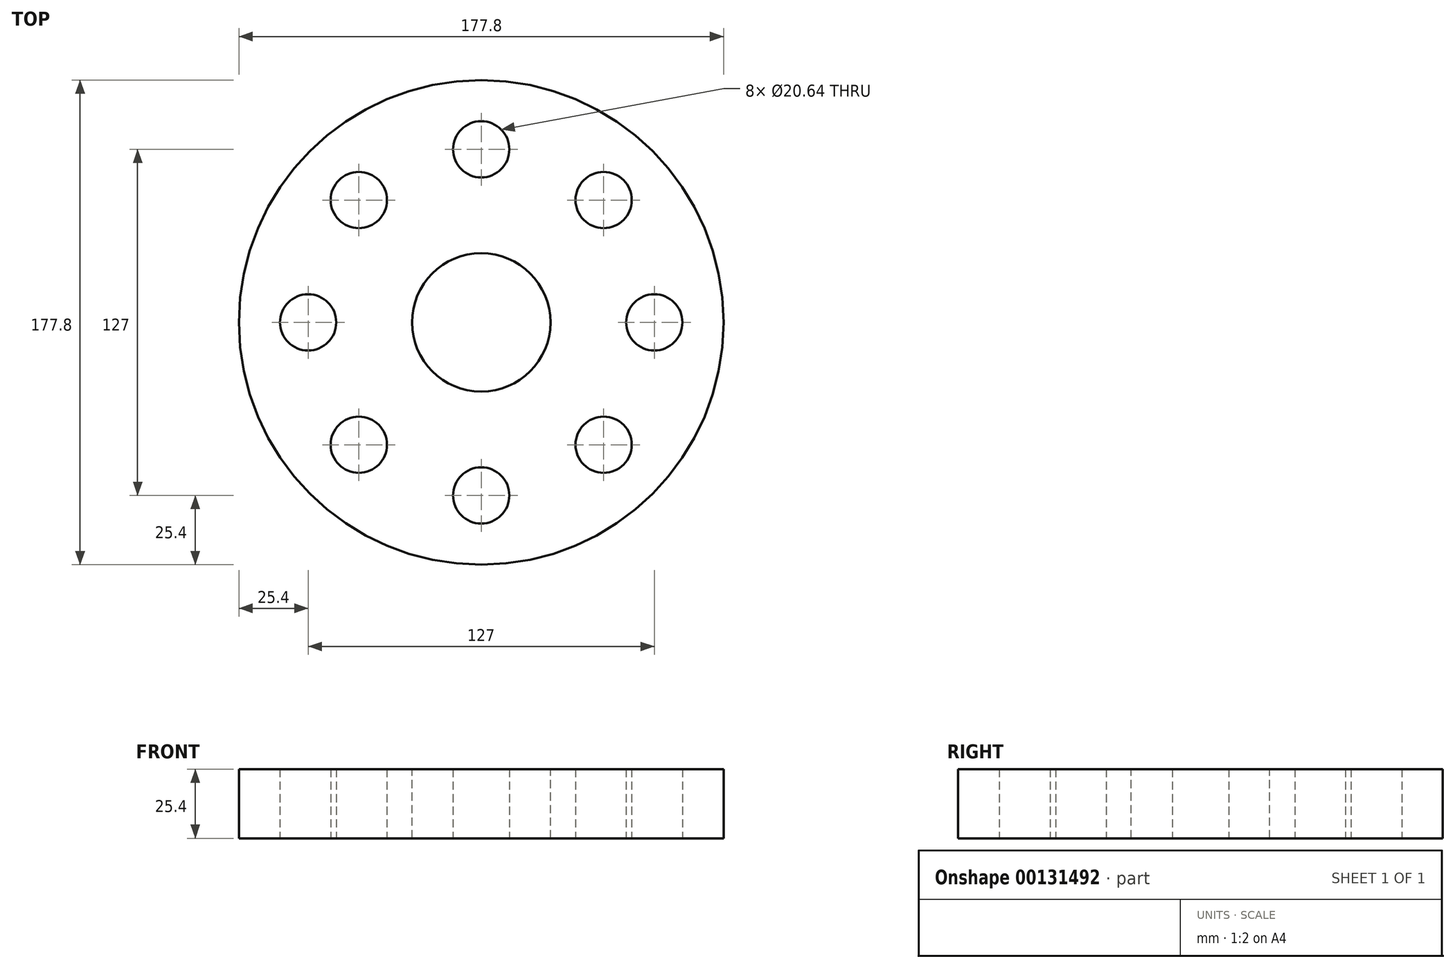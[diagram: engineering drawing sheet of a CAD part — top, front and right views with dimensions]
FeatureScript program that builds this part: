
annotation { "Feature Type Name" : "Feature", "Feature Type Description" : "" }
export const myFeature = defineFeature(function(context is Context, id is Id, definition is map)
    precondition{}
    {
        {
            var Q0;
            Q0=qCreatedBy(makeId("Top.planeOp"),FACE);
            var sketch = newSketch(context, id + "F0", { "sketchPlane" : qUnion([Q0])});
            skCircle(sketch, "E0", {"center": v(0, 0) * mm, "radius": 88.9 * mm});
            skPoint(sketch, "E1", {"position": v(0, 63.5) * mm});
            skPoint(sketch, "E2.1.0", {"position": v(-44.9, 44.9) * mm});
            skPoint(sketch, "E2.2.0", {"position": v(-63.5, 0) * mm});
            skPoint(sketch, "E3.0.3.0", {"position": v(-44.9, -44.9) * mm});
            skPoint(sketch, "E3.0.4.0", {"position": v(0, -63.5) * mm});
            skPoint(sketch, "E3.0.5.0", {"position": v(44.9, -44.9) * mm});
            skPoint(sketch, "E3.0.6.0", {"position": v(63.5, 0) * mm});
            skPoint(sketch, "E3.0.7.0", {"position": v(44.9, 44.9) * mm});
            skSolve(sketch);
        }
        {
            var Q0;
            Q0 = qSketchRegion(id + "F0", true);
            extrude(context, id + "F1", {"entities" : qUnion([Q0]), "depth" : 25.4 * mm});
        }
        {
            var Q0;
            Q0=sQuery(id+"F0.wireOp",VERTEX,"895da96b-3355-4bea-800d-bb29986c0918.1.0");
            var Q1;
            Q1=sQuery(id+"F0.wireOp",VERTEX,"E1");
            var Q2;
            Q2=sQuery(id+"F0.wireOp",VERTEX,"54c976e0-06ee-42b3-b940-04180ae81c69.0.7.0");
            var Q3;
            Q3=sQuery(id+"F0.wireOp",VERTEX,"54c976e0-06ee-42b3-b940-04180ae81c69.0.6.0");
            var Q4;
            Q4=sQuery(id+"F0.wireOp",VERTEX,"4e21a561-bfc3-4077-ada8-399f0a8686c4.0.5.0");
            var Q5;
            Q5=sQuery(id+"F0.wireOp",VERTEX,"4e21a561-bfc3-4077-ada8-399f0a8686c4.0.4.0");
            var Q6;
            Q6=sQuery(id+"F0.wireOp",VERTEX,"4e21a561-bfc3-4077-ada8-399f0a8686c4.0.3.0");
            var Q7;
            Q7=sQuery(id+"F0.wireOp",VERTEX,"895da96b-3355-4bea-800d-bb29986c0918.2.0");
            var Q8;
            Q8=sQuery(id+"F0.wireOp",VERTEX,"b7afe19b-5001-41d6-be3d-2ed2f612f88f.7.0");
            var Q9;
            Q9=sQuery(id+"F0.wireOp",VERTEX,"b7afe19b-5001-41d6-be3d-2ed2f612f88f.6.0");
            var Q10;
            Q10=sQuery(id+"F0.wireOp",VERTEX,"b7afe19b-5001-41d6-be3d-2ed2f612f88f.4.0");
            var Q11;
            Q11=sQuery(id+"F0.wireOp",VERTEX,"b7afe19b-5001-41d6-be3d-2ed2f612f88f.5.0");
            var Q12;
            Q12=sQuery(id+"F0.wireOp",VERTEX,"b7afe19b-5001-41d6-be3d-2ed2f612f88f.3.0");
            var Q13;
            Q13=sQuery(id+"F0.wireOp",VERTEX,"b7afe19b-5001-41d6-be3d-2ed2f612f88f.2.0");
            var Q14;
            Q14=sQuery(id+"F0.wireOp",VERTEX,"b7afe19b-5001-41d6-be3d-2ed2f612f88f.1.0");
            var Q15;
            Q15=sQuery(id+"F0.wireOp",VERTEX,"E2.1.0");
            var Q16;
            Q16=sQuery(id+"F0.wireOp",VERTEX,"E2.2.0");
            var Q17;
            Q17=sQuery(id+"F0.wireOp",VERTEX,"E3.0.3.0");
            var Q18;
            Q18=sQuery(id+"F0.wireOp",VERTEX,"E3.0.5.0");
            var Q19;
            Q19=sQuery(id+"F0.wireOp",VERTEX,"E3.0.4.0");
            var Q20;
            Q20=sQuery(id+"F0.wireOp",VERTEX,"E3.0.6.0");
            var Q21;
            Q21=sQuery(id+"F0.wireOp",VERTEX,"E3.0.7.0");
            var Q22;
            Q22=makeQuery(id+"F1.opExtrude","SWEPT_BODY",BODY,{"disambiguationData":[OSD([sQuery(id+"F0.wireOp",EDGE,"E0")])]});
            hole(context, id + "F2", {"style" : HoleStyle.SIMPLE, "endStyle" : HoleEndStyle.THROUGH, "oppositeDirection" : true, "standardTappedOrClearance" : lookupTablePath({ "standard" : "ANSI", "engagement" : "75%", "pitch" : "14 tpi", "size" : "7/8", "type" : "Tapped" }), "standardBlindInLast" : lookupTablePath({ "standard" : "ANSI", "engagement" : "75%", "pitch" : "14 tpi", "size" : "7/8", "type" : "Tapped" }), "holeDiameter" : 20.64 * mm, "locations" : qUnion([Q0, Q1, Q2, Q3, Q4, Q5, Q6, Q7, Q8, Q9, Q10, Q11, Q12, Q13, Q14, Q15, Q16, Q17, Q18, Q19, Q20, Q21]), "scope" : qUnion([Q22]), "isTappedThrough" : true, "majorDiameter" : 22.23 * mm, "showTappedDepth" : true});
        }
        {
            var Q0;
            Q0=makeQuery(id+"F1.opExtrude","CAP_FACE",FACE,{"disambiguationData":[OSD([sQuery(id+"F0.wireOp",EDGE,"E0")])],"isStart":false});
            var sketch = newSketch(context, id + "F3", { "sketchPlane" : qUnion([Q0])});
            skPoint(sketch, "E4", {"position": v(0, 0) * mm});
            skSolve(sketch);
        }
        {
            var Q0;
            Q0=sQuery(id+"F3.wireOp",VERTEX,"E4");
            var Q1;
            Q1=makeQuery(id+"F1.opExtrude","SWEPT_BODY",BODY,{"disambiguationData":[OSD([sQuery(id+"F0.wireOp",EDGE,"E0")])]});
            hole(context, id + "F4", {"style" : HoleStyle.SIMPLE, "endStyle" : HoleEndStyle.THROUGH, "holeDiameter" : 50.8 * mm, "locations" : qUnion([Q0]), "scope" : qUnion([Q1]), "isTappedThrough" : true});
        }
    });
